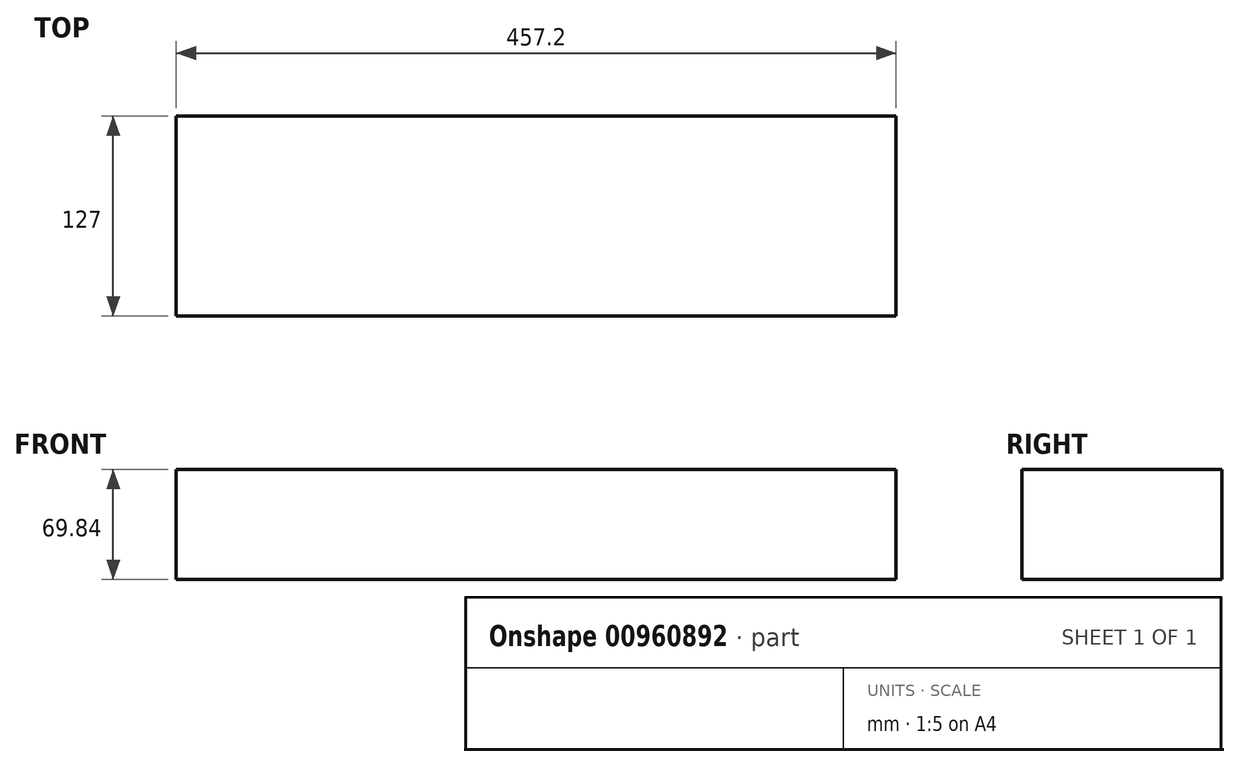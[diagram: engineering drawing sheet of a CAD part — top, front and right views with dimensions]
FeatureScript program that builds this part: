
annotation { "Feature Type Name" : "Feature", "Feature Type Description" : "" }
export const myFeature = defineFeature(function(context is Context, id is Id, definition is map)
    precondition{}
    {
        {
            var Q0;
            Q0=qCreatedBy(makeId("Front.planeOp"),FACE);
            var sketch = newSketch(context, id + "F0", { "sketchPlane" : qUnion([Q0])});
            skLineSegment(sketch, "E0.bottom", {"start": v(-228.6, -34.93) * mm, "end": v(228.6, -34.93) * mm});
            skLineSegment(sketch, "E0.top", {"start": v(-228.6, 34.93) * mm, "end": v(228.6, 34.93) * mm});
            skLineSegment(sketch, "E0.left", {"start": v(-228.6, -34.93) * mm, "end": v(-228.6, 34.93) * mm});
            skLineSegment(sketch, "E0.right", {"start": v(228.6, -34.93) * mm, "end": v(228.6, 34.93) * mm});
            skPoint(sketch, "E0.middle", {"position": v(0, 0) * mm});
            skSolve(sketch);
        }
        {
            var Q0;
            Q0 = qSketchRegion(id + "F0", true);
            extrude(context, id + "F1", {"entities" : qUnion([Q0]), "oppositeDirection" : true, "depth" : 127 * mm, "offsetDistance" : 25.4 * mm});
        }
    });
